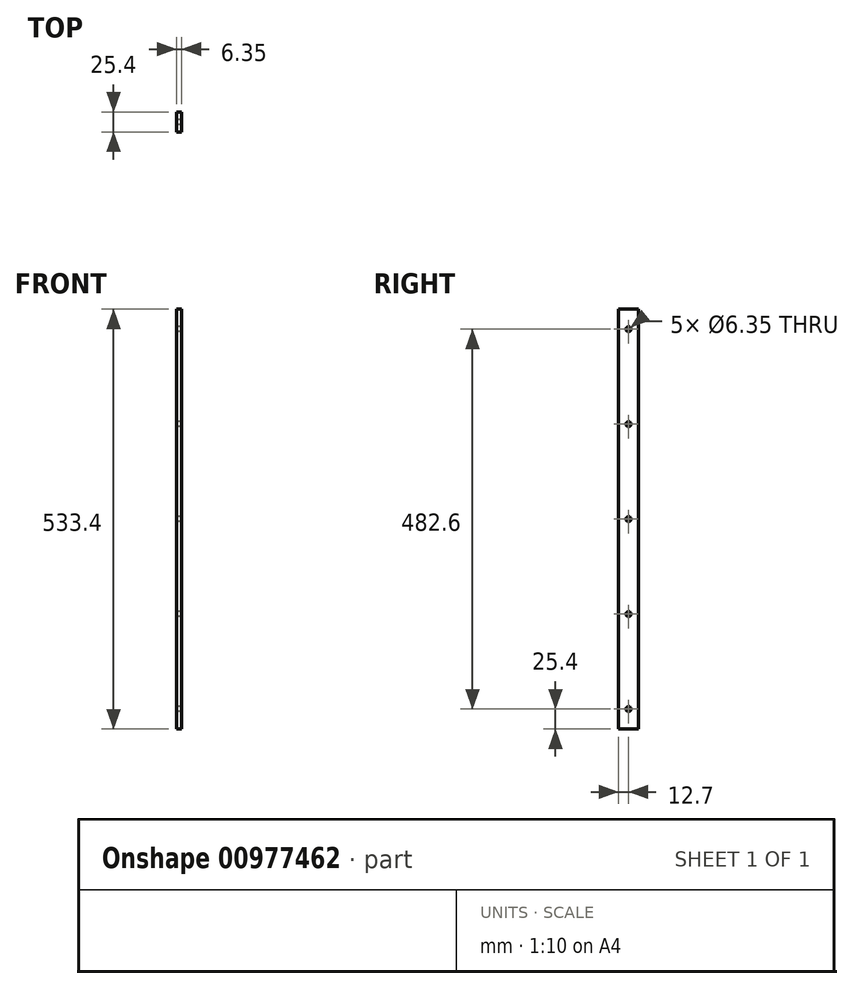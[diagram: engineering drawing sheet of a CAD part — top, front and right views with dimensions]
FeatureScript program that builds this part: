
annotation { "Feature Type Name" : "Feature", "Feature Type Description" : "" }
export const myFeature = defineFeature(function(context is Context, id is Id, definition is map)
    precondition{}
    {
        {
            var Q0;
            Q0=qCreatedBy(makeId("Right.planeOp"),FACE);
            var sketch = newSketch(context, id + "F0", { "sketchPlane" : qUnion([Q0])});
            skLineSegment(sketch, "E0.bottom", {"start": v(12.7, 266.7) * mm, "end": v(-12.7, 266.7) * mm});
            skLineSegment(sketch, "E0.top", {"start": v(12.7, -266.7) * mm, "end": v(-12.7, -266.7) * mm});
            skLineSegment(sketch, "E0.left", {"start": v(12.7, 266.7) * mm, "end": v(12.7, -266.7) * mm});
            skLineSegment(sketch, "E0.right", {"start": v(-12.7, 266.7) * mm, "end": v(-12.7, -266.7) * mm});
            skPoint(sketch, "E0.middle", {"position": v(0, 0) * mm});
            skCircle(sketch, "E1", {"center": v(0, 0) * mm, "radius": 3.18 * mm});
            skCircle(sketch, "E2", {"center": v(0, -120.65) * mm, "radius": 3.18 * mm});
            skCircle(sketch, "E3", {"center": v(0, -241.3) * mm, "radius": 3.18 * mm});
            skCircle(sketch, "E4", {"center": v(0, 120.65) * mm, "radius": 3.18 * mm});
            skCircle(sketch, "E5", {"center": v(0, 241.3) * mm, "radius": 3.18 * mm});
            skSolve(sketch);
        }
        {
            var Q0;
            Q0 = qSketchRegion(id + "F0", true);
            extrude(context, id + "F1", {"entities" : qUnion([Q0]), "depth" : 6.35 * mm, "offsetDistance" : 25.4 * mm});
        }
    });
